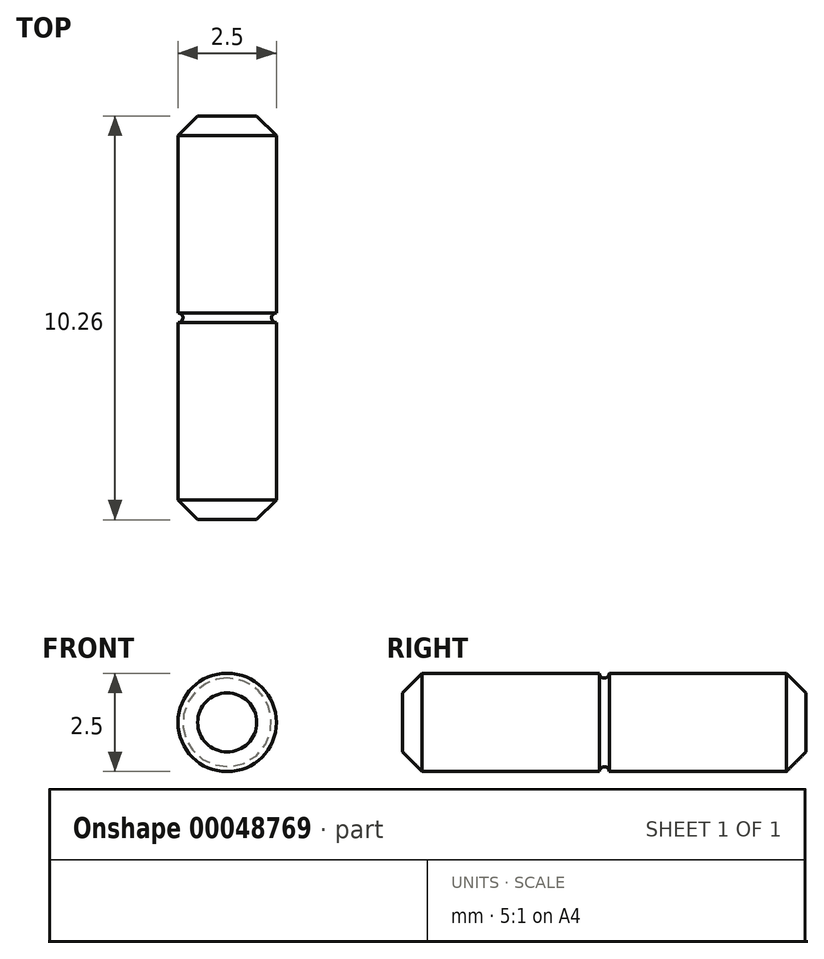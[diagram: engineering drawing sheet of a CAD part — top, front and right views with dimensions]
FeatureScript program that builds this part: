
annotation { "Feature Type Name" : "Feature", "Feature Type Description" : "" }
export const myFeature = defineFeature(function(context is Context, id is Id, definition is map)
    precondition{}
    {
        {
            var Q0;
            Q0=qCreatedBy(makeId("Right.planeOp"),FACE);
            var sketch = newSketch(context, id + "F0", { "sketchPlane" : qUnion([Q0])});
            skLineSegment(sketch, "E0", {"start": v(0, 0) * mm, "end": v(0, 1.13) * mm});
            skPoint(sketch, "E1", {"position": v(0, 1.25) * mm});
            skArc(sketch, "E2", {"start": v(0, 1.13) * mm, "mid": v(-0.09, 1.16) * mm, "end": v(-0.12, 1.25) * mm});
            skLineSegment(sketch, "E3", {"start": v(-0.12, 1.25) * mm, "end": v(-5.12, 1.25) * mm});
            skLineSegment(sketch, "E4", {"start": v(-5.12, 1.25) * mm, "end": v(-5.12, 0) * mm});
            skLineSegment(sketch, "E5", {"start": v(-5.12, 0) * mm, "end": v(0, 0) * mm});
            skArc(sketch, "E6.MirrorCS", {"start": v(0, 1.13) * mm, "mid": v(0.09, 1.16) * mm, "end": v(0.12, 1.25) * mm});
            skLineSegment(sketch, "E7.MirrorCS", {"start": v(0.13, 1.25) * mm, "end": v(5.12, 1.25) * mm});
            skLineSegment(sketch, "E8.MirrorCS", {"start": v(5.12, 1.25) * mm, "end": v(5.12, 0) * mm});
            skLineSegment(sketch, "E9.MirrorCS", {"start": v(5.12, 0) * mm, "end": v(0, 0) * mm});
            skSolve(sketch);
        }
        {
            var Q0;
            Q0=makeQuery(id+"F0.imprint","IMPRINT",FACE,{"disambiguationData":[TD([[makeQuery(id+"F0.imprint","IMPRINT",EDGE,{"derivedFrom":sQuery(id+"F0.wireOp",EDGE,"E0")}),1.0]])]});
            var Q1;
            Q1=makeQuery(id+"F0.imprint","IMPRINT",FACE,{"disambiguationData":[TD([[makeQuery(id+"F0.imprint","IMPRINT",EDGE,{"derivedFrom":sQuery(id+"F0.wireOp",EDGE,"E0")}),-1.0]])]});
            var Q2;
            Q2=sQuery(id+"F0.wireOp",EDGE,"E9.MirrorCS");
            revolve(context, id + "F1", {"entities" : qUnion([Q0, Q1]), "axis" : qUnion([Q2]), "revolveType" : RevolveType.FULL});
        }
        {
            var Q0;
            Q0=makeQuery(id+"F1.opRevolve","SWEPT_EDGE",EDGE,{"disambiguationData":[OSD([sQuery(id+"F0.wireOp",EDGE,"E3"),sQuery(id+"F0.wireOp",EDGE,"E4")])]});
            var Q1;
            Q1=makeQuery(id+"F1.opRevolve","SWEPT_EDGE",EDGE,{"disambiguationData":[OSD([sQuery(id+"F0.wireOp",EDGE,"E7.MirrorCS"),sQuery(id+"F0.wireOp",EDGE,"E8.MirrorCS")])]});
            chamfer(context, id + "F2", {"entities" : qUnion([Q0, Q1]), "width" : 0.5 * mm, "tangentPropagation" : true});
        }
    });
